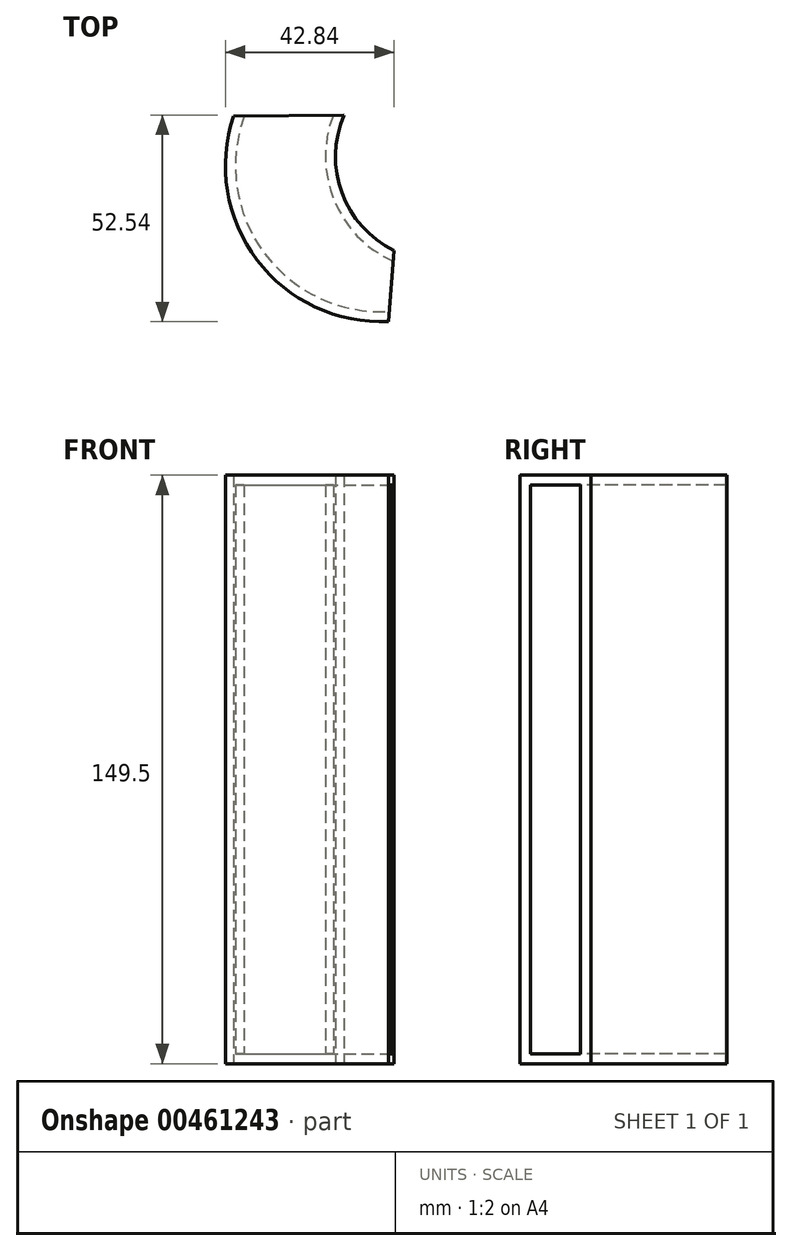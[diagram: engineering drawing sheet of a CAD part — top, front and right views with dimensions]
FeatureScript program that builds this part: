
annotation { "Feature Type Name" : "Feature", "Feature Type Description" : "" }
export const myFeature = defineFeature(function(context is Context, id is Id, definition is map)
    precondition{}
    {
        {
            var Q0;
            Q0=qCreatedBy(makeId("Top.planeOp"),FACE);
            var sketch = newSketch(context, id + "F0", { "sketchPlane" : qUnion([Q0])});
            skArc(sketch, "E0", {"start": v(-60.24, 22.8) * mm, "mid": v(-54.3, -13.7) * mm, "end": v(-20.82, -29.37) * mm});
            skArc(sketch, "E1", {"start": v(-32.13, 23.12) * mm, "mid": v(-32.72, 3.35) * mm, "end": v(-19.47, -11.34) * mm});
            skLineSegment(sketch, "E2", {"start": v(-60.24, 22.8) * mm, "end": v(-32.13, 23.12) * mm});
            skLineSegment(sketch, "E3", {"start": v(-19.47, -11.34) * mm, "end": v(-20.82, -29.37) * mm});
            skSolve(sketch);
        }
        {
            var Q0;
            Q0=qSketchRegion(id+"F0",true);
            extrude(context, id + "F1", {"entities" : qUnion([Q0]), "depth" : 149.5 * mm});
        }
        {
            var Q0;
            Q0=makeQuery(id+"F1.opExtrude","SWEPT_FACE",FACE,{"disambiguationData":[OSD([sQuery(id+"F0.wireOp",EDGE,"E2")])]});
            var Q1;
            Q1=makeQuery(id+"F1.opExtrude","SWEPT_FACE",FACE,{"disambiguationData":[OSD([sQuery(id+"F0.wireOp",EDGE,"E3")])]});
            shell(context, id + "F2", {"entities" : qUnion([Q0, Q1]), "thickness" : 2.54 * mm});
        }
    });
